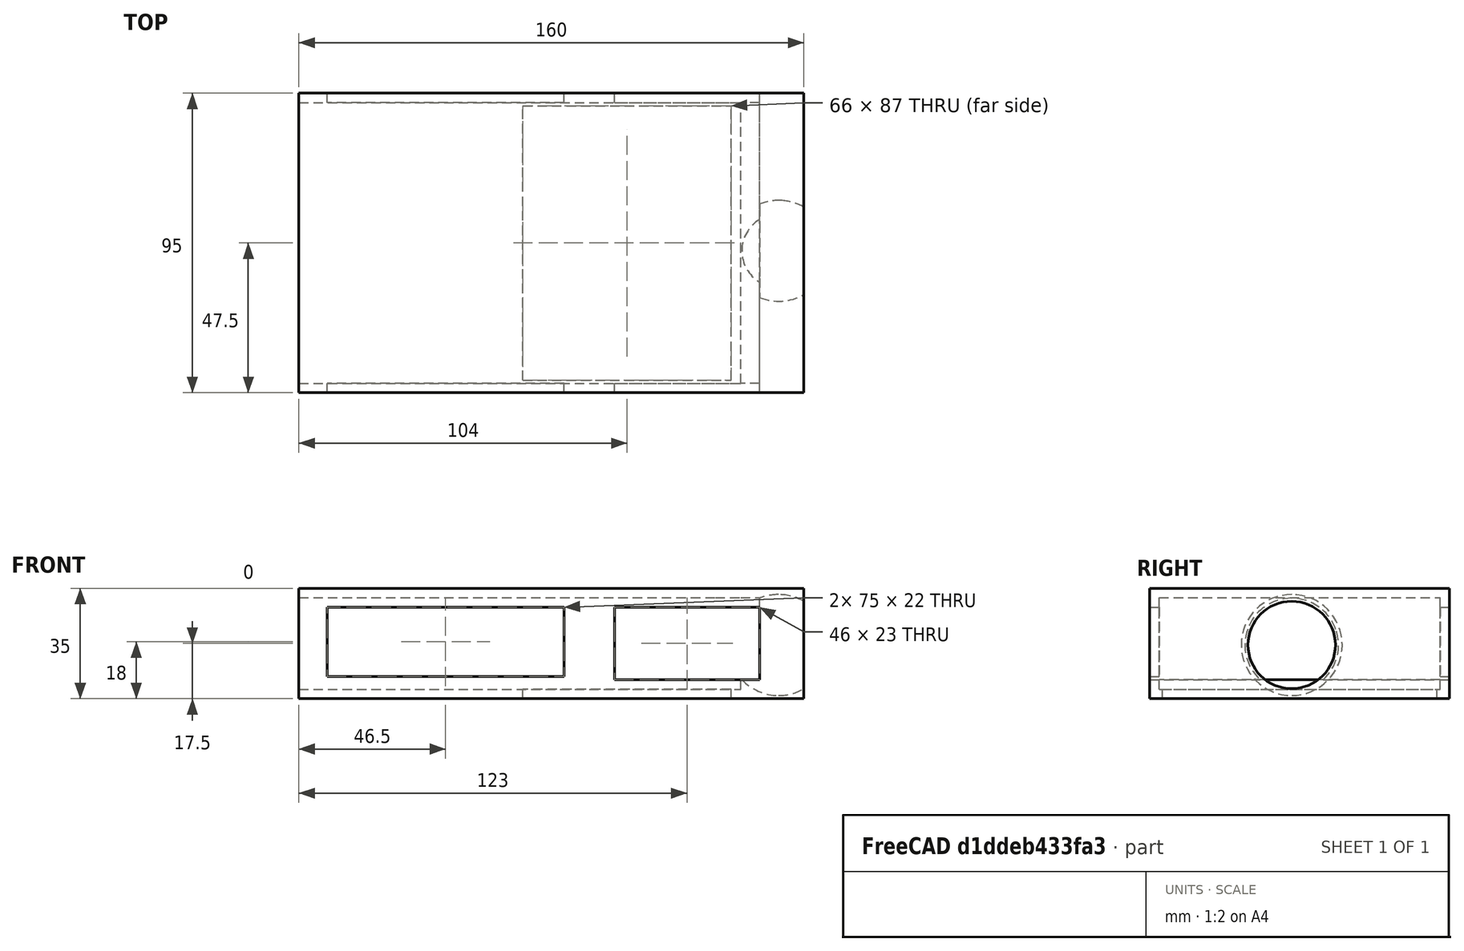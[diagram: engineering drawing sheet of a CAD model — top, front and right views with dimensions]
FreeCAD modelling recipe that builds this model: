
FCSTD DOCUMENT  (FreeCAD 0.20R29410 (Git))
Label: base
License: All rights reserved
LicenseURL: http://en.wikipedia.org/wiki/All_rights_reserved
objects: Part::Box×6, Part::Cut×6, Part::Sphere×1
note: 13 computed .brp shape members not serialized (recipe doc carries the construction recipe); baked Part::Feature solids carry a one-line shape summary decoded from their .brp

FEATURE [Part::Box] Box  label="Cubo"
  AttacherType = Attacher::AttachEngine3D
  Height = 35
  Length = 160
  Width = 95
FEATURE [Part::Box] Box001  label="Cubo001"
  AttacherType = Attacher::AttachEngine3D
  Height = 22
  Length = 75
  Placement = pos=(9,0,7) rot=(0,0,1;0rad)
  Width = 150
FEATURE [Part::Cut] Cut
  Base = -> Box
  Tool = -> Box001
FEATURE [Part::Box] Box002  label="Cubo002"
  AttacherType = Attacher::AttachEngine3D
  Height = 29
  Length = 140
  Placement = pos=(0,3,3) rot=(0,0,1;0rad)
  Width = 89
FEATURE [Part::Cut] Cut001
  Base = -> Cut
  Tool = -> Box002
FEATURE [Part::Sphere] Sphere  label="Esfera"
  Angle1 = -90
  Angle2 = 90
  Angle3 = 360
  AttacherType = Attacher::AttachEngine3D
  Placement = pos=(152,45,17) rot=(0,0,1;0rad)
  Radius = 16
FEATURE [Part::Cut] Cut002
  Base = -> Cut001
  Tool = -> Sphere
FEATURE [Part::Box] Box003  label="Cubo003"
  AttacherType = Attacher::AttachEngine3D
  Height = 10
  Length = 66
  Placement = pos=(71,4,0) rot=(0,0,1;0rad)
  Width = 87
FEATURE [Part::Cut] Cut003
  Base = -> Cut002
  Tool = -> Box003
FEATURE [Part::Box] Box004  label="Cubo004"
  AttacherType = Attacher::AttachEngine3D
  Height = 23
  Length = 46
  Placement = pos=(100,-4,6) rot=(0,0,1;0rad)
  Width = 130
FEATURE [Part::Cut] Cut004
  Base = -> Cut003
  Tool = -> Box004
FEATURE [Part::Box] Box005  label="Cubo005"
  AttacherType = Attacher::AttachEngine3D
  Height = 10
  Length = 14
  Placement = pos=(132,3,22) rot=(0,0,1;0rad)
  Width = 89
FEATURE [Part::Cut] Cut005
  Base = -> Cut004
  Tool = -> Box005
